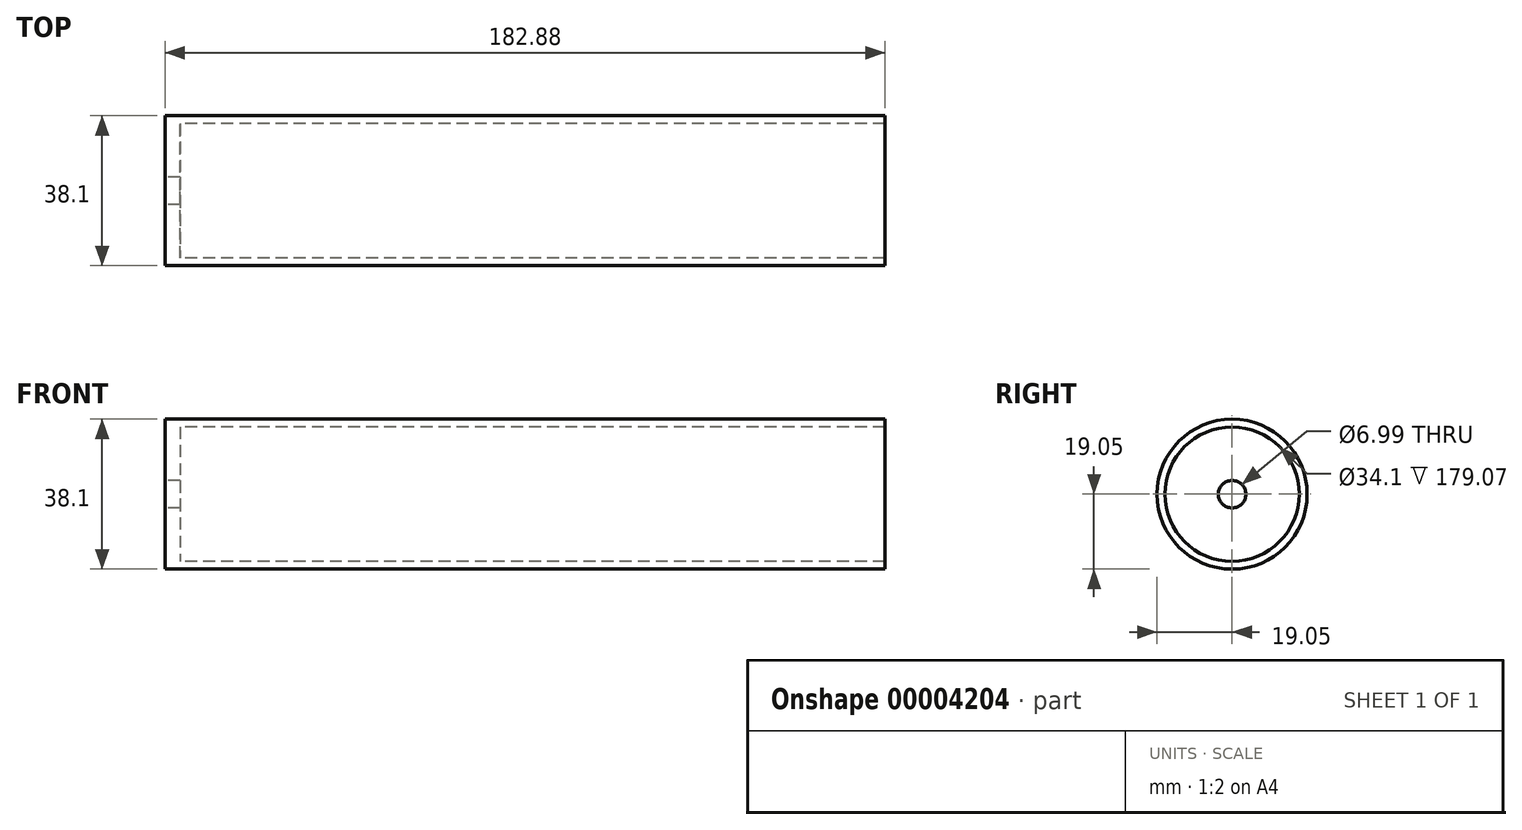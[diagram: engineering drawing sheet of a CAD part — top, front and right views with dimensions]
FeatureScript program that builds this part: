
annotation { "Feature Type Name" : "Feature", "Feature Type Description" : "" }
export const myFeature = defineFeature(function(context is Context, id is Id, definition is map)
    precondition{}
    {
        {
            var Q0;
            Q0=qCreatedBy(makeId("Front.planeOp"),FACE);
            var sketch = newSketch(context, id + "F0", { "sketchPlane" : qUnion([Q0])});
            skLineSegment(sketch, "E0", {"start": v(0, 19.05) * mm, "end": v(179.07, 19.05) * mm});
            skLineSegment(sketch, "E1", {"start": v(0, 17.05) * mm, "end": v(179.07, 17.05) * mm});
            skLineSegment(sketch, "E2", {"start": v(179.07, 17.05) * mm, "end": v(179.07, 19.05) * mm});
            skLineSegment(sketch, "E3", {"start": v(0, 0) * mm, "end": v(97.62, 0) * mm});
            skLineSegment(sketch, "E4", {"start": v(-3.81, 19.05) * mm, "end": v(0, 19.05) * mm});
            skLineSegment(sketch, "E5", {"start": v(-3.81, 3.5) * mm, "end": v(0, 3.5) * mm});
            skLineSegment(sketch, "E6", {"start": v(0, 3.5) * mm, "end": v(0, 17.05) * mm});
            skLineSegment(sketch, "E7", {"start": v(-3.81, 19.05) * mm, "end": v(-3.81, 3.5) * mm});
            skLineSegment(sketch, "E8", {"start": v(179.07, 19.05) * mm, "end": v(192.92, 5.2) * mm});
            skSolve(sketch);
        }
        {
            var Q0;
            Q0=makeQuery(id+"F0.imprint","IMPRINT",FACE,{"disambiguationData":[TD([[makeQuery(id+"F0.imprint","IMPRINT",EDGE,{"derivedFrom":sQuery(id+"F0.wireOp",EDGE,"E0")}),-1.0]])]});
            var Q1;
            Q1=sQuery(id+"F0.wireOp",EDGE,"E3");
            revolve(context, id + "F1", {"entities" : qUnion([Q0]), "axis" : qUnion([Q1]), "revolveType" : RevolveType.FULL});
        }
    });
